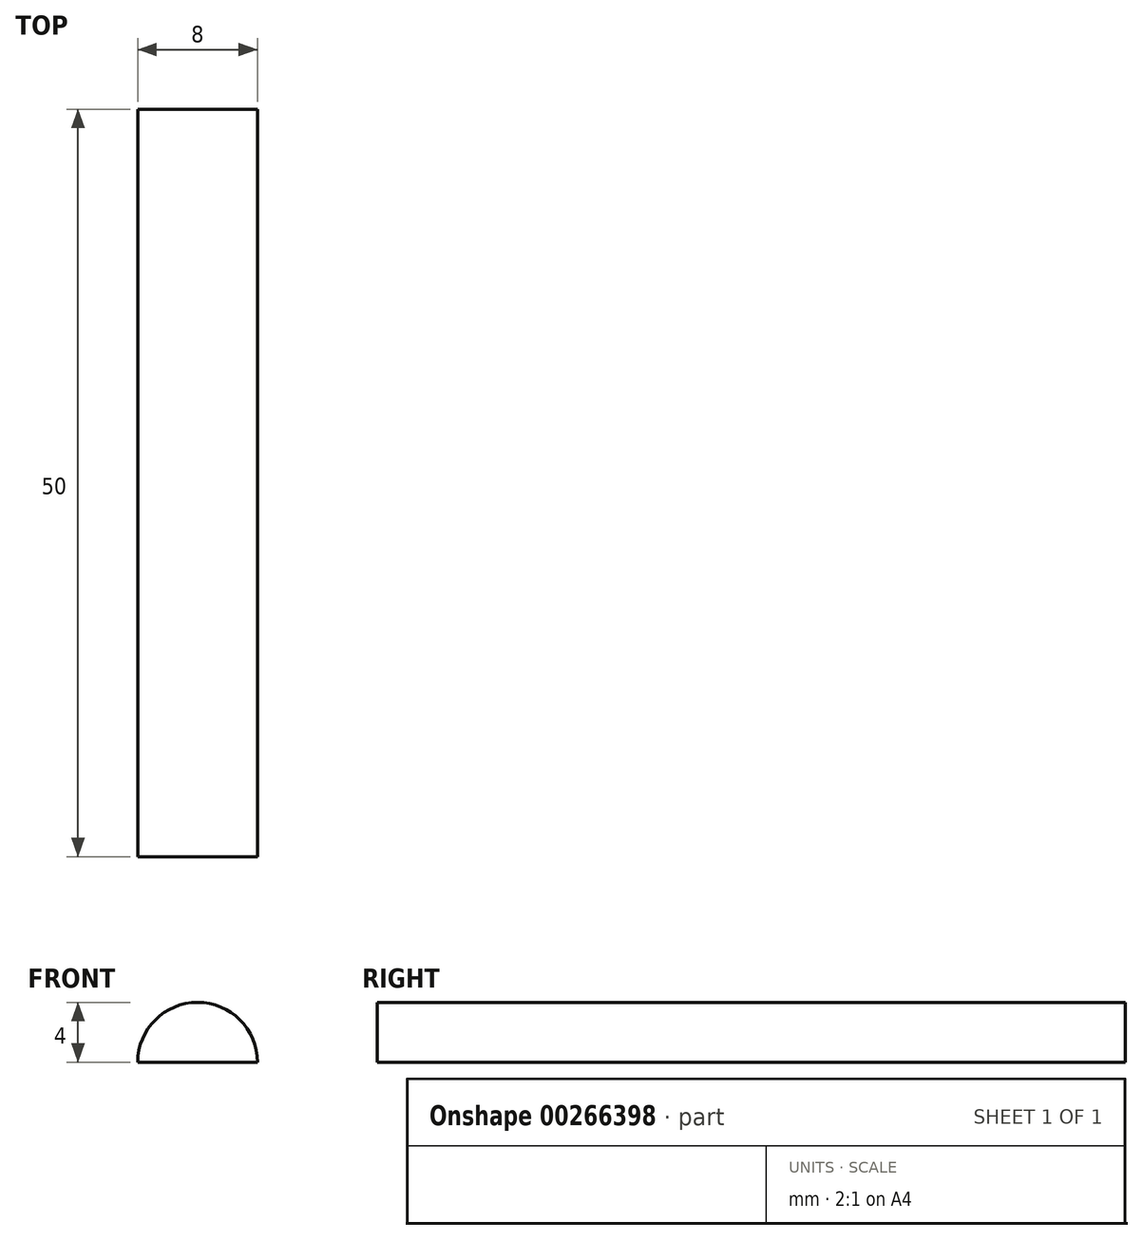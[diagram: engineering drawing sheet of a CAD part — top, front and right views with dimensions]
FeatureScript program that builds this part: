
annotation { "Feature Type Name" : "Feature", "Feature Type Description" : "" }
export const myFeature = defineFeature(function(context is Context, id is Id, definition is map)
    precondition{}
    {
        {
            var Q0;
            Q0=qCreatedBy(makeId("Top.planeOp"),FACE);
            var sketch = newSketch(context, id + "F0", { "sketchPlane" : qUnion([Q0])});
            skLineSegment(sketch, "E0.bottom", {"start": v(4, -25) * mm, "end": v(-4, -25) * mm});
            skLineSegment(sketch, "E0.top", {"start": v(4, 25) * mm, "end": v(-4, 25) * mm});
            skLineSegment(sketch, "E0.left", {"start": v(4, -25) * mm, "end": v(4, 25) * mm});
            skLineSegment(sketch, "E0.right", {"start": v(-4, -25) * mm, "end": v(-4, 25) * mm});
            skPoint(sketch, "E0.middle", {"position": v(0, 0) * mm});
            skLineSegment(sketch, "E1", {"start": v(0, 25) * mm, "end": v(0, -25) * mm});
            skSolve(sketch);
        }
        {
            var Q0;
            {var subQ0=sQuery(id+"F0.wireOp",EDGE,"E0.left");Q0=makeQuery(id+"F0.imprint","IMPRINT",FACE,{"disambiguationData":[TD([[makeQuery(id+"F0.imprint","IMPRINT",EDGE,{"derivedFrom":subQ0}),1.0]])]});}
            var Q1;
            Q1=sQuery(id+"F0.wireOp",EDGE,"E1");
            revolve(context, id + "F1", {"entities" : qUnion([Q0]), "axis" : qUnion([Q1]), "revolveType" : RevolveType.ONE_DIRECTION, "angle" : 180 * degree});
        }
    });
